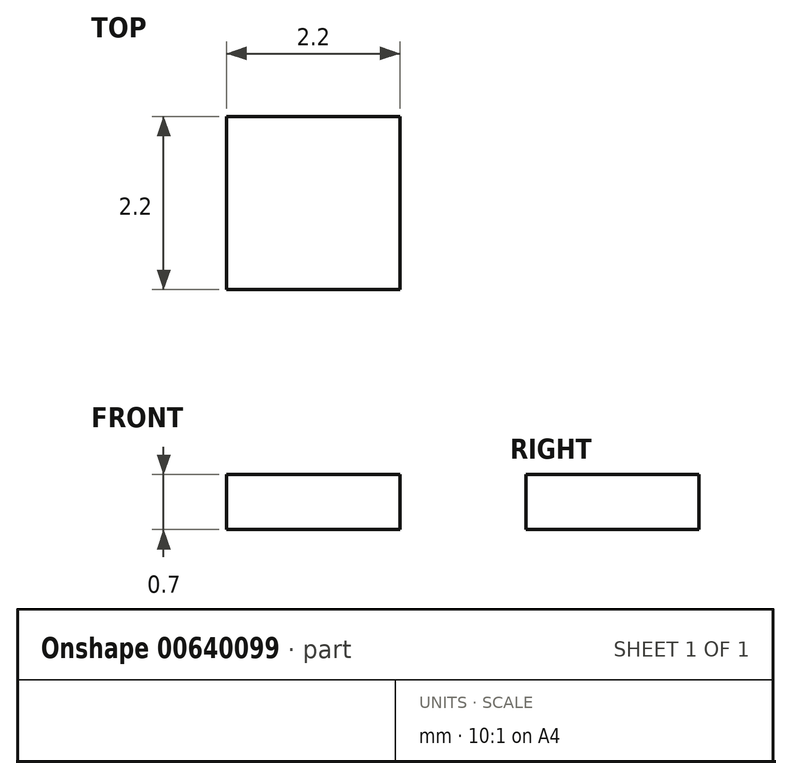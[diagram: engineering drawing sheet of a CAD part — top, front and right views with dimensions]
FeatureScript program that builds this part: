
annotation { "Feature Type Name" : "Feature", "Feature Type Description" : "" }
export const myFeature = defineFeature(function(context is Context, id is Id, definition is map)
    precondition{}
    {
        {
            var Q0;
            Q0=qCreatedBy(makeId("Top.planeOp"),FACE);
            var sketch = newSketch(context, id + "F0", { "sketchPlane" : qUnion([Q0])});
            skLineSegment(sketch, "E0.bottom", {"start": v(1.1, 1.1) * mm, "end": v(-1.1, 1.1) * mm});
            skLineSegment(sketch, "E0.top", {"start": v(1.1, -1.1) * mm, "end": v(-1.1, -1.1) * mm});
            skLineSegment(sketch, "E0.left", {"start": v(1.1, 1.1) * mm, "end": v(1.1, -1.1) * mm});
            skLineSegment(sketch, "E0.right", {"start": v(-1.1, 1.1) * mm, "end": v(-1.1, -1.1) * mm});
            skPoint(sketch, "E0.middle", {"position": v(0, 0) * mm});
            skSolve(sketch);
        }
        {
            var Q0;
            Q0=makeQuery(id+"F0.imprint","IMPRINT",FACE,{"disambiguationData":[TD([[makeQuery(id+"F0.imprint","IMPRINT",EDGE,{"derivedFrom":sQuery(id+"F0.wireOp",EDGE,"E0.bottom")}),1.0]])]});
            extrude(context, id + "F1", {"entities" : qUnion([Q0]), "depth" : .7 * mm, "offsetDistance" : 25 * mm});
        }
    });
